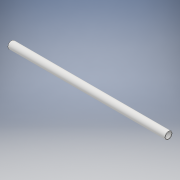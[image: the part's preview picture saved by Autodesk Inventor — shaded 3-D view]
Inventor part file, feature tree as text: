
AUTODESK INVENTOR PART (.ipt)
format: ipt  version: 2018 (Build 220112000, 112)  size: 95,744 bytes
history: native  units: mm
features: extrude x1, sketch x1
ambient origin geometry x8: Origin, YZ Plane, XZ Plane, XY Plane, X Axis, Y Axis, Z Axis, Center Point
bodies: Solid1 (feature_tree)
feature tree (2):
  extrude  "Extrusion1"  Depth=914.4mm
  sketch  "Sketch1"  dims[d0=42.164mm d1=35.052mm d2=914.4mm d3=0.0mm]
